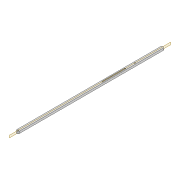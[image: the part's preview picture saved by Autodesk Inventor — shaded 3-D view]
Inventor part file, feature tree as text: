
AUTODESK INVENTOR PART (.ipt)
format: ipt  version: 2022 (Build 260153000, 153)  size: 117,248 bytes
history: native  units: mm
features: extrude x2, sketch x2, projected_geometry x1
ambient origin geometry x8: Origin, YZ Plane, XZ Plane, XY Plane, X Axis, Y Axis, Z Axis, Center Point
bodies: Solid1 (feature_tree)
feature tree (5):
  extrude  "Extrusion1"  Depth=343.336mm
  extrude  "Extrusion2"  Depth=3.0mm
  sketch  "Sketch1"  dims[d0=8.0mm d1=343.336mm]
  sketch  "Sketch3"  dims[d2=3.0mm d3=3.0mm d4=6.0mm d5=0.0mm d14=3.0mm d15=27.9mm d16=95.0mm d17=8.0mm d18=80.0mm d21=4.363323mm d22=4.363323mm d23=100.0mm d24=0.0mm]
  projected_geometry  "Projected Loop1"
